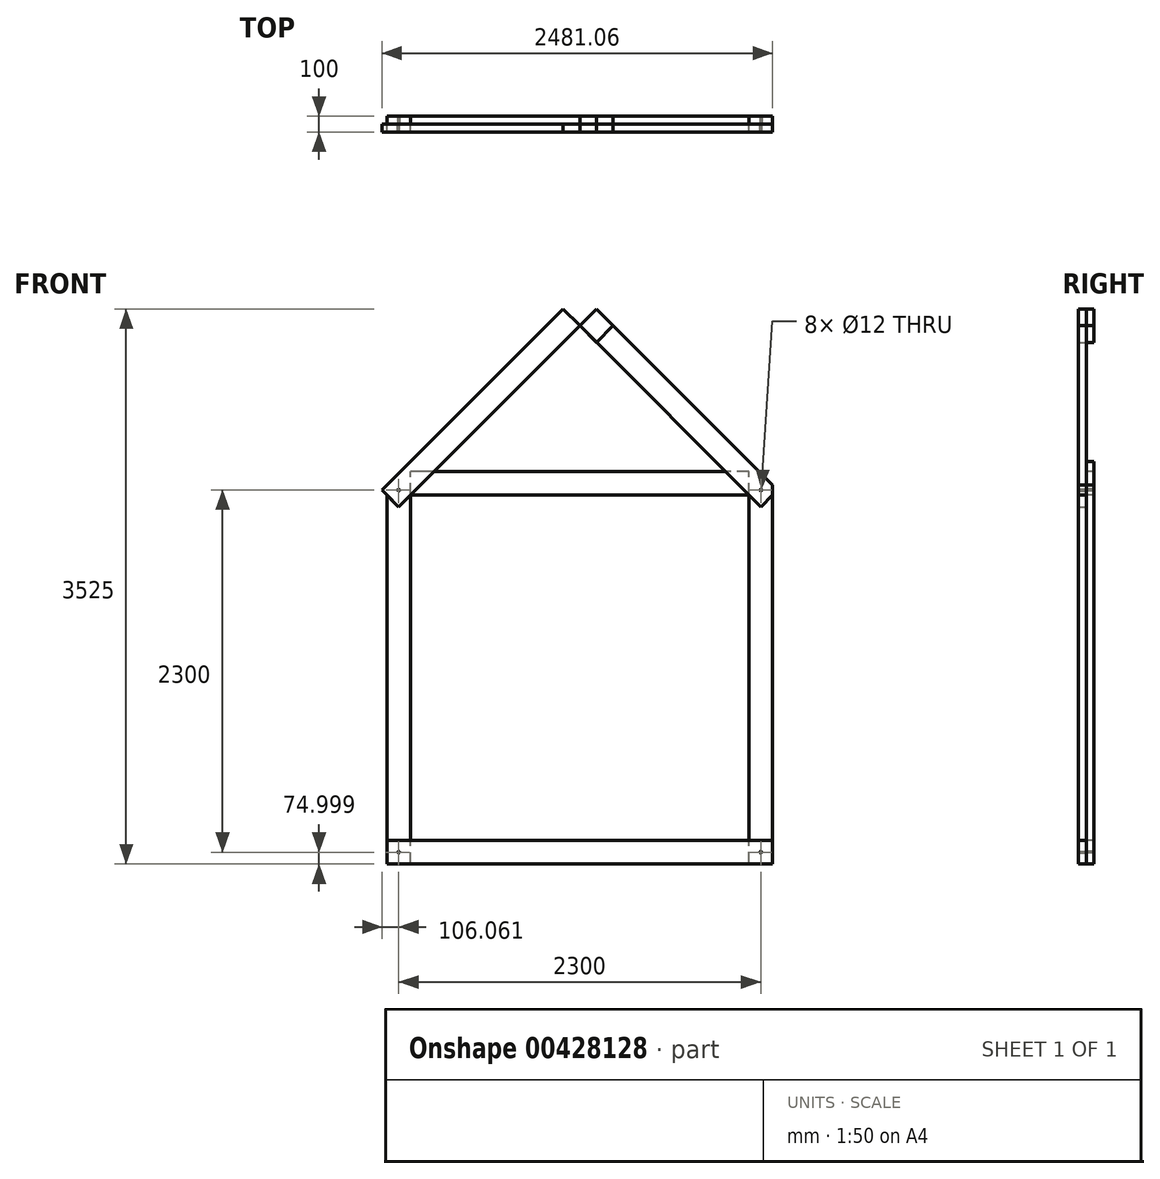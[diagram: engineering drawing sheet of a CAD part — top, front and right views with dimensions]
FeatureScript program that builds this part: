
annotation { "Feature Type Name" : "Feature", "Feature Type Description" : "" }
export const myFeature = defineFeature(function(context is Context, id is Id, definition is map)
    precondition{}
    {
        {
            var Q0;
            Q0=qCreatedBy(makeId("Front.planeOp"),FACE);
            var sketch = newSketch(context, id + "F0", { "sketchPlane" : qUnion([Q0])});
            skLineSegment(sketch, "E0", {"start": v(-1198.4, -297.42) * mm, "end": v(-1198.4, 2002.58) * mm, "construction": true});
            skLineSegment(sketch, "E1", {"start": v(-1198.4, 2002.58) * mm, "end": v(-48.4, 3152.58) * mm, "construction": true});
            skLineSegment(sketch, "E2.bottom", {"start": v(-1123.4, -372.42) * mm, "end": v(-1273.4, -372.42) * mm});
            skLineSegment(sketch, "E2.top", {"start": v(-1123.4, -222.42) * mm, "end": v(-1273.4, -222.42) * mm});
            skLineSegment(sketch, "E2.left", {"start": v(-1123.4, -372.42) * mm, "end": v(-1123.4, -222.42) * mm});
            skLineSegment(sketch, "E2.right", {"start": v(-1273.4, -372.42) * mm, "end": v(-1273.4, -222.42) * mm});
            skPoint(sketch, "E2.middle", {"position": v(-1198.4, -297.42) * mm});
            skLineSegment(sketch, "E3.bottom", {"start": v(1176.6, -372.42) * mm, "end": v(1026.6, -372.42) * mm});
            skLineSegment(sketch, "E3.top", {"start": v(1176.6, -222.42) * mm, "end": v(1026.6, -222.42) * mm});
            skLineSegment(sketch, "E3.left", {"start": v(1176.6, -372.42) * mm, "end": v(1176.6, -222.42) * mm});
            skPoint(sketch, "E3.middle", {"position": v(1101.6, -297.42) * mm});
            skLineSegment(sketch, "E4", {"start": v(-1123.4, -222.42) * mm, "end": v(1026.6, -222.42) * mm});
            skLineSegment(sketch, "E5", {"start": v(-1123.4, -372.42) * mm, "end": v(1026.6, -372.42) * mm});
            skLineSegment(sketch, "E6.bottom", {"start": v(-1123.4, 1927.58) * mm, "end": v(-1273.4, 1927.58) * mm, "construction": true});
            skLineSegment(sketch, "E6.top", {"start": v(-1123.4, 2077.58) * mm, "end": v(-1273.4, 2077.58) * mm});
            skLineSegment(sketch, "E6.left", {"start": v(-1123.4, 1927.58) * mm, "end": v(-1123.4, 2077.58) * mm});
            skLineSegment(sketch, "E6.right", {"start": v(-1273.4, 1927.58) * mm, "end": v(-1273.4, 2077.58) * mm});
            skPoint(sketch, "E6.middle", {"position": v(-1198.4, 2002.58) * mm});
            skLineSegment(sketch, "E7", {"start": v(-48.4, 3152.58) * mm, "end": v(4.62, 3205.61) * mm, "construction": true});
            skLineSegment(sketch, "E8", {"start": v(4.62, 3205.61) * mm, "end": v(-48.4, 3152.58) * mm, "construction": true});
            skLineSegment(sketch, "E9", {"start": v(-48.4, 3152.58) * mm, "end": v(-101.44, 3205.61) * mm, "construction": true});
            skLineSegment(sketch, "E10", {"start": v(-101.44, 3205.61) * mm, "end": v(-48.4, 3258.65) * mm});
            skLineSegment(sketch, "E11", {"start": v(-48.4, 3258.65) * mm, "end": v(57.66, 3152.58) * mm});
            skLineSegment(sketch, "E12", {"start": v(57.66, 3152.58) * mm, "end": v(-1145.38, 1949.55) * mm});
            skLineSegment(sketch, "E13", {"start": v(-1198.4, 2002.58) * mm, "end": v(-1251.44, 2055.61) * mm, "construction": true});
            skLineSegment(sketch, "E14", {"start": v(-1198.4, 2002.58) * mm, "end": v(-1145.38, 1949.55) * mm, "construction": true});
            skLineSegment(sketch, "E15", {"start": v(-1251.44, 2055.61) * mm, "end": v(-1304.47, 2002.58) * mm});
            skLineSegment(sketch, "E16", {"start": v(-1304.47, 2002.58) * mm, "end": v(-1198.4, 1896.51) * mm});
            skLineSegment(sketch, "E17", {"start": v(-1198.4, 1896.51) * mm, "end": v(-1145.38, 1949.55) * mm});
            skLineSegment(sketch, "E18", {"start": v(-1251.44, 2055.61) * mm, "end": v(-101.44, 3205.61) * mm});
            skLineSegment(sketch, "E19", {"start": v(-1273.4, 1927.58) * mm, "end": v(-1273.4, -222.42) * mm});
            skLineSegment(sketch, "E20", {"start": v(-1123.4, -222.42) * mm, "end": v(-1123.4, 1927.58) * mm});
            skLineSegment(sketch, "E21", {"start": v(-48.4, -372.42) * mm, "end": v(-48.4, 3600.7) * mm, "construction": true});
            skLineSegment(sketch, "E22.MirrorCS", {"start": v(1207.66, 2002.58) * mm, "end": v(1101.6, 1896.51) * mm});
            skLineSegment(sketch, "E23.MirrorCS", {"start": v(1176.6, 1927.58) * mm, "end": v(1176.6, 2077.58) * mm});
            skLineSegment(sketch, "E24.MirrorCS", {"start": v(1101.6, 2002.58) * mm, "end": v(1154.62, 2055.61) * mm, "construction": true});
            skLineSegment(sketch, "E25.MirrorCS", {"start": v(1154.62, 2055.61) * mm, "end": v(1207.66, 2002.58) * mm});
            skLineSegment(sketch, "E26.MirrorCS", {"start": v(1101.6, 2002.58) * mm, "end": v(1048.56, 1949.55) * mm, "construction": true});
            skLineSegment(sketch, "E27.MirrorCS", {"start": v(1026.6, 2077.58) * mm, "end": v(1176.6, 2077.58) * mm});
            skLineSegment(sketch, "E28.MirrorCS", {"start": v(1026.6, 1927.58) * mm, "end": v(1176.6, 1927.58) * mm, "construction": true});
            skLineSegment(sketch, "E29.MirrorCS", {"start": v(1101.6, 1896.51) * mm, "end": v(1048.56, 1949.55) * mm});
            skLineSegment(sketch, "E30.MirrorCS", {"start": v(1026.6, 1927.58) * mm, "end": v(1026.6, 2077.58) * mm});
            skLineSegment(sketch, "E31.MirrorCS", {"start": v(1026.6, -372.42) * mm, "end": v(1026.6, -222.42) * mm});
            skLineSegment(sketch, "E32.MirrorCS", {"start": v(1026.6, -222.42) * mm, "end": v(1176.6, -222.42) * mm});
            skLineSegment(sketch, "E33.MirrorCS", {"start": v(1026.6, -372.42) * mm, "end": v(1176.6, -372.42) * mm});
            skLineSegment(sketch, "E34.MirrorCS", {"start": v(-48.4, 3258.65) * mm, "end": v(-154.47, 3152.58) * mm});
            skLineSegment(sketch, "E35.MirrorCS", {"start": v(4.62, 3205.61) * mm, "end": v(-48.4, 3258.65) * mm});
            skLineSegment(sketch, "E36.MirrorCS", {"start": v(-101.44, 3205.61) * mm, "end": v(-48.4, 3152.58) * mm, "construction": true});
            skLineSegment(sketch, "E37.MirrorCS", {"start": v(-1273.4, -372.42) * mm, "end": v(-1123.4, -372.42) * mm});
            skLineSegment(sketch, "E38.MirrorCS", {"start": v(-1273.4, -222.42) * mm, "end": v(-1123.4, -222.42) * mm});
            skPoint(sketch, "E39.MirrorP", {"position": v(1101.6, 2002.58) * mm});
            skLineSegment(sketch, "E40.MirrorCS", {"start": v(1154.62, 2055.61) * mm, "end": v(4.62, 3205.61) * mm});
            skLineSegment(sketch, "E41.MirrorCS", {"start": v(1026.6, -222.42) * mm, "end": v(1026.6, 1927.58) * mm});
            skLineSegment(sketch, "E42.MirrorCS", {"start": v(1101.6, 2002.58) * mm, "end": v(-48.4, 3152.58) * mm, "construction": true});
            skLineSegment(sketch, "E43.MirrorCS", {"start": v(1101.6, -297.42) * mm, "end": v(1101.6, 2002.58) * mm, "construction": true});
            skLineSegment(sketch, "E44.MirrorCS", {"start": v(1176.6, 1927.58) * mm, "end": v(1176.6, -222.42) * mm});
            skLineSegment(sketch, "E45.MirrorCS", {"start": v(-154.47, 3152.58) * mm, "end": v(1048.56, 1949.55) * mm});
            skLineSegment(sketch, "E46.MirrorCS", {"start": v(1026.6, -222.42) * mm, "end": v(-1123.4, -222.42) * mm});
            skLineSegment(sketch, "E47.MirrorCS", {"start": v(1026.6, -372.42) * mm, "end": v(-1123.4, -372.42) * mm});
            skCircle(sketch, "E48", {"center": v(-1198.4, 2002.58) * mm, "radius": 6 * mm});
            skCircle(sketch, "E49", {"center": v(-48.4, 3152.58) * mm, "radius": 6 * mm});
            skCircle(sketch, "E50", {"center": v(1101.6, 2002.58) * mm, "radius": 6 * mm});
            skCircle(sketch, "E51", {"center": v(1101.6, -297.42) * mm, "radius": 6 * mm});
            skCircle(sketch, "E52", {"center": v(-1198.4, -297.42) * mm, "radius": 6 * mm});
            skLineSegment(sketch, "E53", {"start": v(1026.6, 2077.58) * mm, "end": v(1026.6, 2183.65) * mm});
            skLineSegment(sketch, "E54", {"start": v(1026.6, 2183.65) * mm, "end": v(1176.6, 2183.65) * mm});
            skLineSegment(sketch, "E55", {"start": v(1176.6, 2183.65) * mm, "end": v(1176.6, 2077.58) * mm});
            skLineSegment(sketch, "E56", {"start": v(-1123.4, 2077.58) * mm, "end": v(-1123.4, 2183.65) * mm});
            skLineSegment(sketch, "E57", {"start": v(-1123.4, 2183.65) * mm, "end": v(-1273.4, 2183.65) * mm});
            skLineSegment(sketch, "E58", {"start": v(-1273.4, 2183.65) * mm, "end": v(-1273.4, 2077.58) * mm});
            skLineSegment(sketch, "E59.bottom", {"start": v(1026.6, 1927.58) * mm, "end": v(1026.6, 1927.58) * mm});
            skLineSegment(sketch, "E59.top", {"start": v(1026.6, 2077.58) * mm, "end": v(1026.6, 2077.58) * mm});
            skLineSegment(sketch, "E60.left", {"start": v(-1123.4, 2077.58) * mm, "end": v(-1123.4, 1927.58) * mm});
            skLineSegment(sketch, "E60.right", {"start": v(1026.6, 2077.58) * mm, "end": v(1026.6, 1927.58) * mm});
            skLineSegment(sketch, "E61", {"start": v(163.72, 3046.51) * mm, "end": v(57.66, 2940.45) * mm});
            skLineSegment(sketch, "E62", {"start": v(1026.6, 1971.51) * mm, "end": v(-1123.4, 1971.51) * mm});
            skLineSegment(sketch, "E63", {"start": v(1026.6, 2121.51) * mm, "end": v(-1123.4, 2121.51) * mm});
            skSolve(sketch);
        }
        {
            var Q0;
            {var subQ0=sQuery(id+"F0.wireOp",EDGE,"E53");Q0=makeQuery(id+"F0.imprint","IMPRINT",FACE,{"disambiguationData":[TD([[makeQuery(id+"F0.imprint","IMPRINT",EDGE,{"derivedFrom":subQ0}),-1.0]])]});}
            var Q1;
            {var subQ11=sQuery(id+"F0.wireOp",EDGE,"E29.MirrorCS");Q1=makeQuery(id+"F0.imprint","IMPRINT",FACE,{"disambiguationData":[TD([[makeQuery(id+"F0.imprint","IMPRINT",EDGE,{"derivedFrom":subQ11}),-1.0]])]});}
            var Q2;
            {var subQ0=sQuery(id+"F0.wireOp",EDGE,"E29.MirrorCS");Q2=makeQuery(id+"F0.imprint","IMPRINT",FACE,{"disambiguationData":[TD([[makeQuery(id+"F0.imprint","IMPRINT",EDGE,{"derivedFrom":subQ0}),1.0]])]});}
            var Q3;
            Q3=makeQuery(id+"F0.imprint","IMPRINT",FACE,{"disambiguationData":[TD([[makeQuery(id+"F0.imprint","IMPRINT",EDGE,{"derivedFrom":sQuery(id+"F0.wireOp",EDGE,"E31.MirrorCS")}),-1.0]])]});
            var Q4;
            Q4=makeQuery(id+"F0.imprint","IMPRINT",FACE,{"disambiguationData":[TD([[makeQuery(id+"F0.imprint","IMPRINT",EDGE,{"derivedFrom":sQuery(id+"F0.wireOp",EDGE,"E2.left")}),1.0]])]});
            var Q5;
            {var subQ0=sQuery(id+"F0.wireOp",EDGE,"E17");Q5=makeQuery(id+"F0.imprint","IMPRINT",FACE,{"disambiguationData":[TD([[makeQuery(id+"F0.imprint","IMPRINT",EDGE,{"derivedFrom":subQ0}),-1.0]])]});}
            var Q6;
            {var subQ0=sQuery(id+"F0.wireOp",EDGE,"E56");Q6=makeQuery(id+"F0.imprint","IMPRINT",FACE,{"disambiguationData":[TD([[makeQuery(id+"F0.imprint","IMPRINT",EDGE,{"derivedFrom":subQ0}),1.0]])]});}
            var Q7;
            {var subQ5=sQuery(id+"F0.wireOp",EDGE,"E17");Q7=makeQuery(id+"F0.imprint","IMPRINT",FACE,{"disambiguationData":[TD([[makeQuery(id+"F0.imprint","IMPRINT",EDGE,{"derivedFrom":subQ5}),1.0]])]});}
            extrude(context, id + "F1", {"entities" : qUnion([Q0, Q1, Q2, Q3, Q4, Q5, Q6, Q7]), "depth" : -50 * mm});
        }
        {
            var Q0;
            {var subQ0=sQuery(id+"F0.wireOp",EDGE,"E45.MirrorCS");var subQ3=sQuery(id+"F0.wireOp",EDGE,"E12");var subQ4=makeQuery(id+"F0.imprint","INTERSECT",VERTEX,{"derivedFrom":[subQ3,subQ0]});Q0=makeQuery(id+"F0.imprint","IMPRINT",FACE,{"disambiguationData":[TD([[makeQuery(id+"F0.imprint","IMPRINT",EDGE,{"disambiguationData":[TD([[subQ4,-1.0]])],"derivedFrom":subQ3}),-1.0]])]});}
            var Q1;
            {var subQ4=sQuery(id+"F0.wireOp",EDGE,"E34.MirrorCS");Q1=makeQuery(id+"F0.imprint","IMPRINT",FACE,{"disambiguationData":[TD([[makeQuery(id+"F0.imprint","IMPRINT",EDGE,{"derivedFrom":subQ4}),1.0]])]});}
            var Q2;
            {var subQ3=sQuery(id+"F0.wireOp",EDGE,"E12");var subQ5=sQuery(id+"F0.wireOp",EDGE,"Eojktbgq-gnKO-uqMG-sPAW-VTWSaUcgMlM7");var subQ6=makeQuery(id+"F0.imprint","INTERSECT",VERTEX,{"derivedFrom":[subQ3,subQ5]});Q2=makeQuery(id+"F0.imprint","IMPRINT",FACE,{"disambiguationData":[TD([[makeQuery(id+"F0.imprint","IMPRINT",EDGE,{"disambiguationData":[TD([[subQ6,-1.0]])],"derivedFrom":subQ3}),-1.0]])]});}
            var Q3;
            {var subQ1=sQuery(id+"F0.wireOp",EDGE,"E6.top");var subQ3=sQuery(id+"F0.wireOp",EDGE,"E18");var subQ4=makeQuery(id+"F0.imprint","INTERSECT",VERTEX,{"derivedFrom":[subQ1,subQ3]});Q3=makeQuery(id+"F0.imprint","IMPRINT",FACE,{"disambiguationData":[TD([[makeQuery(id+"F0.imprint","IMPRINT",EDGE,{"disambiguationData":[TD([[subQ4,1.0]])],"derivedFrom":subQ1}),-1.0]])]});}
            var Q4;
            {var subQ0=sQuery(id+"F0.wireOp",EDGE,"E17");Q4=makeQuery(id+"F0.imprint","IMPRINT",FACE,{"disambiguationData":[TD([[makeQuery(id+"F0.imprint","IMPRINT",EDGE,{"derivedFrom":subQ0}),1.0]])]});}
            var Q5;
            {var subQ0=sQuery(id+"F0.wireOp",EDGE,"2zTIRHZN-IMxJ-qIkd-V003-hpQcy7ufmjv5");var subQ1=sQuery(id+"F0.wireOp",EDGE,"E12");var subQ2=makeQuery(id+"F0.imprint","INTERSECT",VERTEX,{"derivedFrom":[subQ1,subQ0]});Q5=makeQuery(id+"F0.imprint","IMPRINT",FACE,{"disambiguationData":[TD([[makeQuery(id+"F0.imprint","IMPRINT",EDGE,{"disambiguationData":[TD([[subQ2,-1.0]])],"derivedFrom":subQ1}),-1.0]])]});}
            var Q6;
            {var subQ0=sQuery(id+"F0.wireOp",EDGE,"E16");var subQ1=sQuery(id+"F0.wireOp",EDGE,"E6.right");var subQ2=makeQuery(id+"F0.imprint","INTERSECT",VERTEX,{"derivedFrom":[subQ1,subQ0]});Q6=makeQuery(id+"F0.imprint","IMPRINT",FACE,{"disambiguationData":[TD([[makeQuery(id+"F0.imprint","IMPRINT",EDGE,{"disambiguationData":[TD([[subQ2,-1.0]])],"derivedFrom":subQ1}),1.0]])]});}
            var Q7;
            Q7=makeQuery(id+"F0.imprint","IMPRINT",FACE,{"disambiguationData":[TD([[makeQuery(id+"F0.imprint","IMPRINT",EDGE,{"derivedFrom":sQuery(id+"F0.wireOp",EDGE,"E2.left")}),-1.0]])]});
            var Q8;
            Q8=makeQuery(id+"F0.imprint","IMPRINT",FACE,{"disambiguationData":[TD([[makeQuery(id+"F0.imprint","IMPRINT",EDGE,{"derivedFrom":sQuery(id+"F0.wireOp",EDGE,"E31.MirrorCS")}),-1.0]])]});
            var Q9;
            Q9=makeQuery(id+"F0.imprint","IMPRINT",FACE,{"disambiguationData":[TD([[makeQuery(id+"F0.imprint","IMPRINT",EDGE,{"derivedFrom":sQuery(id+"F0.wireOp",EDGE,"E2.left")}),1.0]])]});
            extrude(context, id + "F2", {"entities" : qUnion([Q0, Q1, Q2, Q3, Q4, Q5, Q6, Q7, Q8, Q9]), "depth" : 50 * mm});
        }
        {
            var Q0;
            {var subQ1=sQuery(id+"F0.wireOp",EDGE,"E40.MirrorCS");var subQ6=sQuery(id+"F0.wireOp",EDGE,"E12");var subQ9=makeQuery(id+"F0.imprint","INTERSECT",VERTEX,{"derivedFrom":[subQ6,subQ1]});Q0=makeQuery(id+"F0.imprint","IMPRINT",FACE,{"disambiguationData":[TD([[makeQuery(id+"F0.imprint","IMPRINT",EDGE,{"disambiguationData":[TD([[subQ9,-1.0]])],"derivedFrom":subQ6}),1.0]])]});}
            extrude(context, id + "F3", {"entities" : qUnion([Q0]), "depth" : 50 * mm});
        }
        {
            var Q0;
            {var subQ4=sQuery(id+"F0.wireOp",EDGE,"E34.MirrorCS");Q0=makeQuery(id+"F0.imprint","IMPRINT",FACE,{"disambiguationData":[TD([[makeQuery(id+"F0.imprint","IMPRINT",EDGE,{"derivedFrom":subQ4}),1.0]])]});}
            var Q1;
            {var subQ5=sQuery(id+"F0.wireOp",EDGE,"E61");Q1=makeQuery(id+"F0.imprint","IMPRINT",FACE,{"disambiguationData":[TD([[makeQuery(id+"F0.imprint","IMPRINT",EDGE,{"derivedFrom":subQ5}),-1.0]])]});}
            extrude(context, id + "F4", {"entities" : qUnion([Q0, Q1]), "depth" : -50 * mm});
        }
        {
            var Q0;
            {var subQ5=sQuery(id+"F0.wireOp",EDGE,"E61");Q0=makeQuery(id+"F0.imprint","IMPRINT",FACE,{"disambiguationData":[TD([[makeQuery(id+"F0.imprint","IMPRINT",EDGE,{"derivedFrom":subQ5}),1.0]])]});}
            var Q1;
            {var subQ5=sQuery(id+"F0.wireOp",EDGE,"E61");Q1=makeQuery(id+"F0.imprint","IMPRINT",FACE,{"disambiguationData":[TD([[makeQuery(id+"F0.imprint","IMPRINT",EDGE,{"derivedFrom":subQ5}),-1.0]])]});}
            var Q2;
            {var subQ4=sQuery(id+"F0.wireOp",EDGE,"E34.MirrorCS");Q2=makeQuery(id+"F0.imprint","IMPRINT",FACE,{"disambiguationData":[TD([[makeQuery(id+"F0.imprint","IMPRINT",EDGE,{"derivedFrom":subQ4}),1.0]])]});}
            var Q3;
            {var subQ1=sQuery(id+"F0.wireOp",EDGE,"E27.MirrorCS");var subQ3=sQuery(id+"F0.wireOp",EDGE,"E40.MirrorCS");var subQ4=makeQuery(id+"F0.imprint","INTERSECT",VERTEX,{"derivedFrom":[subQ1,subQ3]});Q3=makeQuery(id+"F0.imprint","IMPRINT",FACE,{"disambiguationData":[TD([[makeQuery(id+"F0.imprint","IMPRINT",EDGE,{"disambiguationData":[TD([[subQ4,1.0]])],"derivedFrom":subQ1}),1.0]])]});}
            var Q4;
            {var subQ14=sQuery(id+"F0.wireOp",EDGE,"E29.MirrorCS");Q4=makeQuery(id+"F0.imprint","IMPRINT",FACE,{"disambiguationData":[TD([[makeQuery(id+"F0.imprint","IMPRINT",EDGE,{"derivedFrom":subQ14}),-1.0]])]});}
            var Q5;
            {var subQ3=sQuery(id+"F0.wireOp",EDGE,"E45.MirrorCS");var subQ7=sQuery(id+"F0.wireOp",EDGE,"Eojktbgq-gnKO-uqMG-sPAW-VTWSaUcgMlM7");var subQ9=makeQuery(id+"F0.imprint","INTERSECT",VERTEX,{"derivedFrom":[subQ3,subQ7]});Q5=makeQuery(id+"F0.imprint","IMPRINT",FACE,{"disambiguationData":[TD([[makeQuery(id+"F0.imprint","IMPRINT",EDGE,{"disambiguationData":[TD([[subQ9,-1.0]])],"derivedFrom":subQ3}),1.0]])]});}
            var Q6;
            {var subQ0=sQuery(id+"F0.wireOp",EDGE,"2zTIRHZN-IMxJ-qIkd-V003-hpQcy7ufmjv5");var subQ1=sQuery(id+"F0.wireOp",EDGE,"E45.MirrorCS");var subQ2=makeQuery(id+"F0.imprint","INTERSECT",VERTEX,{"derivedFrom":[subQ1,subQ0]});Q6=makeQuery(id+"F0.imprint","IMPRINT",FACE,{"disambiguationData":[TD([[makeQuery(id+"F0.imprint","IMPRINT",EDGE,{"disambiguationData":[TD([[subQ2,-1.0]])],"derivedFrom":subQ1}),1.0]])]});}
            extrude(context, id + "F5", {"entities" : qUnion([Q0, Q1, Q2, Q3, Q4, Q5, Q6]), "depth" : 50 * mm});
        }
        {
            var Q0;
            {var subQ0=sQuery(id+"F0.wireOp",EDGE,"E62");Q0=makeQuery(id+"F0.imprint","IMPRINT",FACE,{"disambiguationData":[TD([[makeQuery(id+"F0.imprint","IMPRINT",EDGE,{"derivedFrom":subQ0}),-1.0]])]});}
            var Q1;
            {var subQ3=sQuery(id+"F0.wireOp",EDGE,"E63");var subQ5=sQuery(id+"F0.wireOp",EDGE,"E53");var subQ7=makeQuery(id+"F0.imprint","INTERSECT",VERTEX,{"derivedFrom":[subQ5,subQ3]});Q1=makeQuery(id+"F0.imprint","IMPRINT",FACE,{"disambiguationData":[TD([[makeQuery(id+"F0.imprint","IMPRINT",EDGE,{"disambiguationData":[TD([[subQ7,-1.0]])],"derivedFrom":subQ3}),1.0]])]});}
            var Q2;
            {var subQ3=sQuery(id+"F0.wireOp",EDGE,"E63");var subQ5=sQuery(id+"F0.wireOp",EDGE,"E56");var subQ7=makeQuery(id+"F0.imprint","INTERSECT",VERTEX,{"derivedFrom":[subQ5,subQ3]});Q2=makeQuery(id+"F0.imprint","IMPRINT",FACE,{"disambiguationData":[TD([[makeQuery(id+"F0.imprint","IMPRINT",EDGE,{"disambiguationData":[TD([[subQ7,1.0]])],"derivedFrom":subQ3}),1.0]])]});}
            var Q3;
            Q3=makeQuery(id+"F0.imprint","IMPRINT",FACE,{"disambiguationData":[TD([[makeQuery(id+"F0.imprint","IMPRINT",EDGE,{"derivedFrom":sQuery(id+"F0.wireOp",EDGE,"E2.left")}),-1.0]])]});
            extrude(context, id + "F6", {"entities" : qUnion([Q0, Q1, Q2, Q3]), "depth" : -50 * mm});
        }
        {
            var Q0;
            {var subQ0=sQuery(id+"F0.wireOp",EDGE,"E17");Q0=makeQuery(id+"F0.imprint","IMPRINT",FACE,{"disambiguationData":[TD([[makeQuery(id+"F0.imprint","IMPRINT",EDGE,{"derivedFrom":subQ0}),-1.0]])]});}
            var Q1;
            {var subQ0=sQuery(id+"F0.wireOp",EDGE,"E29.MirrorCS");Q1=makeQuery(id+"F0.imprint","IMPRINT",FACE,{"disambiguationData":[TD([[makeQuery(id+"F0.imprint","IMPRINT",EDGE,{"derivedFrom":subQ0}),1.0]])]});}
            extrude(context, id + "F7", {"entities" : qUnion([Q0, Q1]), "depth" : 50 * mm});
        }
    });
